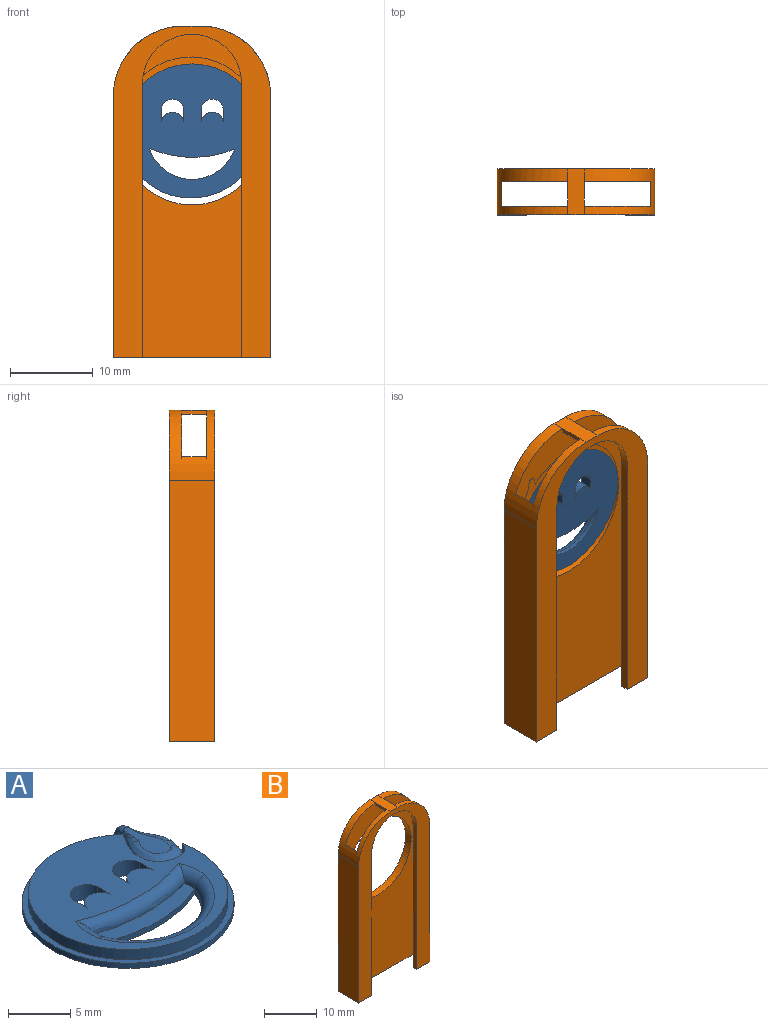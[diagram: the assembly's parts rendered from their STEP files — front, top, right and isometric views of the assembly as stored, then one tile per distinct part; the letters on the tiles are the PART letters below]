
ASSEMBLY  parts=2 mates=1
PART A: 29 faces, bbox 17.5x17.3x2 mm
  f0: cylinder r=8.5mm len=17mm, axis (0,0,-1), area 24.5mm2, adj f3,f4,f17
  f1: plane 16x16mm, normal (0,0,1), area 114.1mm2, adj f5,f6,f7,f8,f9,f10,f11,f12
  f2: plane 4.9x2.08mm, normal (0,0,1), area 5.6mm2, adj f18,f19,f20,f21,f22,f23
  f3: plane 17x17mm, normal (0,0,-1), area 200.8mm2, adj f0,f5,f6,f7,f8,f9,f10,f11
  f4: plane 17.26x17.26mm, normal (0,0,1), area 24.2mm2, adj f0,f16,f18,f19,f22,f23,f28
  f5: cylinder r=1.34mm len=2.65mm, axis (0,0,1), area 5.7mm2, adj f1,f3,f6,f8
  f6: plane 1.57x1.5mm, normal (1,0,0), area 2.4mm2, adj f1,f3,f5,f7
  f7: cylinder r=1.34mm len=2.65mm, axis (0,0,1), area 5.7mm2, adj f1,f3,f6,f8
  f8: plane 1.57x1.5mm, normal (-1,0,0), area 2.4mm2, adj f1,f3,f5,f7
  f9: cylinder r=1.34mm len=2.65mm, axis (0,0,1), area 5.7mm2, adj f1,f3,f10,f12
  f10: plane 1.57x1.5mm, normal (1,0,0), area 2.4mm2, adj f1,f3,f9,f11
  f11: cylinder r=1.34mm len=2.65mm, axis (0,0,1), area 5.7mm2, adj f1,f3,f10,f12
  f12: plane 1.57x1.5mm, normal (-1,0,0), area 2.4mm2, adj f1,f3,f9,f11
  f13: cylinder r=13.3mm len=10.27mm, axis (0,0,1), area 5.3mm2, adj f3,f14,f15
  f14: cylinder r=5.42mm len=10.27mm, axis (0,0,1), area 6.8mm2, adj f3,f13,f26
  f15: plane 10.37x2.36mm, normal (0,0,1), area 14.8mm2, adj f13,f24,f25,f27
  f16: extruded ~5.33x3.74mm, area 8.9mm2, adj f1,f4,f28
  f17: extruded ~4.74x2.49mm, area 3.3mm2, adj f0,f3,f20,f21
  f18: bspline ~4.59x4.44mm, area 10.1mm2, adj f2,f4,f19,f23
  f19: bspline ~1.59x1.3mm, area 1.5mm2, adj f2,f4,f18,f20
  f20: bspline ~1.7x1.2mm, area 2.1mm2, adj f2,f17,f19,f21
  f21: bspline ~3.66x2.22mm, area 6.3mm2, adj f2,f17,f20,f22
  f22: bspline ~1.44x1mm, area 0.6mm2, adj f2,f4,f21,f23
  f23: bspline ~1.5x1mm, area 1.3mm2, adj f2,f4,f18,f22
  f24: torus R=4.46mm, axis (0,0,1), area 2.9mm2, adj f1,f15,f25,f26
  f25: torus R=15.75mm, axis (0,0,1), area 17.7mm2, adj f1,f15,f24,f27
  f26: torus R=6.42mm, axis (0,0,1), area 22.7mm2, adj f1,f14,f24,f27
  f27: torus R=5.32mm, axis (0,0,1), area 3.3mm2, adj f1,f15,f25,f26
  f28: cylinder r=8mm len=16mm, axis (0,0,1), area 45.3mm2, adj f1,f4,f16
PART B: 19 faces, bbox 19x5.5x40 mm
  f0: plane 40x18mm, normal (0,1,0), area 242mm2, adj f2,f5,f7,f10,f11,f12,f13,f14
  f1: plane 40x19mm, normal (0,-1,0), area 276.4mm2, adj f2,f4,f8,f9,f10,f11,f15,f16
  f2: plane 19x5.5mm, normal (0,0,-1), area 38.5mm2, adj f0,f1,f3,f4,f5,f6,f7,f8
  f3: plane 40x19mm, normal (0,1,0), area 502mm2, adj f2,f4,f8,f9,f10,f11,f18
  f4: plane 31.5x5.5mm, normal (-1,0,0), area 173.2mm2, adj f1,f2,f3,f10
  f5: plane 34.37x3mm, normal (1,0,0), area 103.1mm2, adj f0,f2,f6,f10
  f6: plane 40x18mm, normal (0,-1,0), area 467.6mm2, adj f2,f5,f7,f10,f11,f12,f13,f14
  f7: plane 34.37x3mm, normal (-1,0,0), area 103.1mm2, adj f0,f2,f6,f11
  f8: plane 31.5x5.5mm, normal (1,0,0), area 173.2mm2, adj f1,f2,f3,f11
  f9: plane 5.5x2mm, normal (0,0,1), area 11mm2, adj f1,f3,f10,f11,f12,f14
  f10: cylinder r=8.5mm len=8.5mm, axis (0,1,0), area 42.2mm2, adj f0,f1,f3,f4,f5,f6,f9
  f11: cylinder r=8.5mm len=8.5mm, axis (0,-1,0), area 42.2mm2, adj f0,f1,f3,f6,f7,f8,f9
  f12: plane 3x0.5mm, normal (-1,0,0), area 1.5mm2, adj f0,f6,f9,f13
  f13: plane 3x2mm, normal (0,0,-1), area 6mm2, adj f0,f6,f12,f14
  f14: plane 3x0.5mm, normal (1,0,0), area 1.5mm2, adj f0,f6,f9,f13
  f15: plane 33x1mm, normal (1,0,0), area 33mm2, adj f0,f1,f2,f17
  f16: plane 33x1mm, normal (-1,0,0), area 33mm2, adj f0,f1,f2,f17
  f17: cylinder r=6mm len=12mm, axis (0,-1,0), area 18.8mm2, adj f0,f1,f15,f16
  f18: cylinder r=8.5mm len=17mm, axis (0,1,0), area 80.1mm2, adj f3,f6
PLACE A rot(axis=(0,0.71,0.71),180deg) t=(1.37,-4.08,48.11)mm
PLACE B t=(4.83,-19.36,-30.99)mm
MATE fastened A.f14 <-> B.f18  axis (0,-1,0) through (3.46,-4.08,-4.05)mm
